# Revit family: Toilet-Floor_Mount-KOHLER-Corbelle-K-5709
name_source: partatom
category: Plumbing Fixtures
revit_build: Autodesk Revit 2015 (Build: 20140606_1530(x64)
units: mm (PartAtom-declared; Revit-internal decimal feet)

## types (6) — shared parameters
ADA Compliant = Yes
Assembly Code = D2010100
CW Connection = Yes
Cold Water Inlet = Cold Water Inlet
Date Modified = 02/18/2019
Default Elevation = 0"
Description = Corbelle with ContinuousClean Comfort Height two-piece elongated 1.28 gpf toilet with skirted trapway, left-hand trip lever and Revolution 360 swirl flushing technology, seat not included
Flow Rate = 0 GPM
Flush Rate = 1.28GPF
HW Connection = No
Height = 31 5/16"
Hot Water Inlet = Hot Water Inlet
Length = 29 3/8"
Manufacturer = KOHLER Co.
MasterFormat 1995 = 15410
MasterFormat 2004 = 22.41.13
Material = Viterous China
Pressure = 0.00 psi
Product Documentation Link = https://www.us.kohler.com
Product Name = Corbelle
Product Page URL = http://www.us.kohler.com
Rough-In = 12"
Seat Included = No
URL = https://www.us.kohler.com
Vent Connection = No
Waste Connection = Yes
Waste Water Outlet = Waste Water Outlet
WaterSense Certified = Yes
Width = 16 3/8"

## per-type parameters (varying)
| type | Finish | Model | Type |
| 0-White | Kohler-Vitreous_China-0-White | K-5709-0 | 1 |
| 96-Biscuit | Kohler-Vitreous_China-96-Biscuit | K-5709-96 | 2 |
| NY-Dune | Kohler-Vitreous_China-NY-Dune | K-5709-NY | 3 |
| 95-Ice Grey | Kohler-Vitreous_China-95-Ice_Grey | K-5709-95 | 4 |
| G9-Sandbar | Kohler-Vitreous_China-G9-Sandbar | K-5709-G9 | 5 |
| 7-Black Black | Kohler-Vitreous_China-7-Black_Black | K-5709-7 | 6 |

## geometry (parser evidence)
native form markers: Sweep x5
no freeform markers — native parametric forms only
